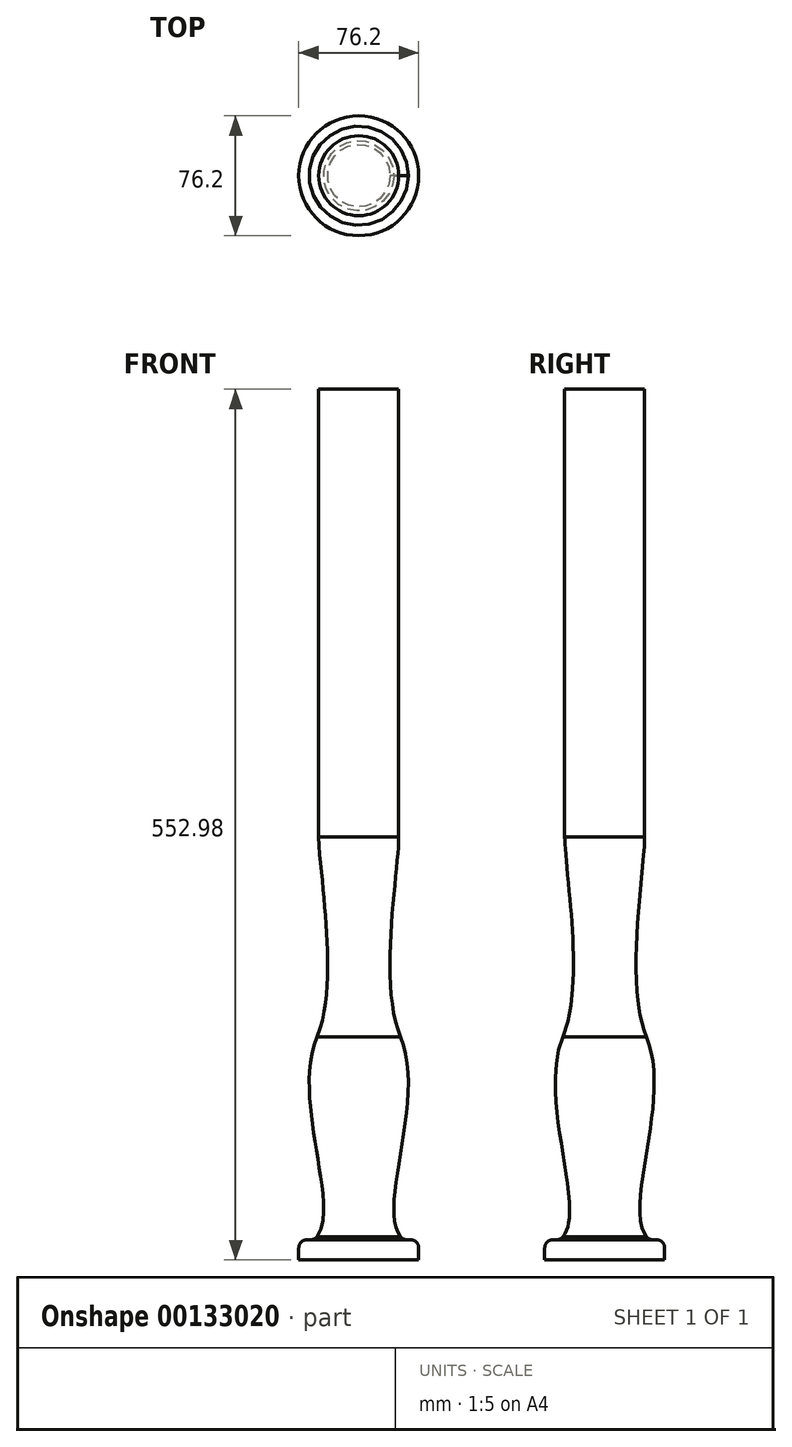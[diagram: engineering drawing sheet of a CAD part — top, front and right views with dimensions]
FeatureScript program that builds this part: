
annotation { "Feature Type Name" : "Feature", "Feature Type Description" : "" }
export const myFeature = defineFeature(function(context is Context, id is Id, definition is map)
    precondition{}
    {
        {
            var Q0;
            Q0=qCreatedBy(makeId("Front.planeOp"),FACE);
            var sketch = newSketch(context, id + "F0", { "sketchPlane" : qUnion([Q0])});
            skLineSegment(sketch, "E0.0", {"start": v(32.98, 284.37) * mm, "end": v(32.98, -255.91) * mm});
            skLineSegment(sketch, "E1", {"start": v(7.58, 284.37) * mm, "end": v(32.98, 284.37) * mm});
            skLineSegment(sketch, "E2.bottom", {"start": v(2.5, -255.91) * mm, "end": v(-0.04, -255.91) * mm});
            skLineSegment(sketch, "E2.top", {"start": v(32.98, -268.61) * mm, "end": v(-5.12, -268.61) * mm});
            skLineSegment(sketch, "E2.left", {"start": v(32.98, -255.91) * mm, "end": v(32.98, -268.61) * mm});
            skLineSegment(sketch, "E2.right", {"start": v(-5.12, -261) * mm, "end": v(-5.12, -268.61) * mm});
            skPoint(sketch, "E3.visualSharp", {"position": v(-5.12, -255.91) * mm});
            skArc(sketch, "E3.filletArc", {"start": v(-0.04, -255.91) * mm, "mid": v(-3.64, -257.4) * mm, "end": v(-5.12, -261) * mm});
            skPoint(sketch, "E4.newPointA", {"position": v(32.98, -255.91) * mm});
            skPoint(sketch, "E4.newPointB", {"position": v(-59.9, -321.48) * mm});
            skArc(sketch, "E4.filletArc", {"start": v(2.5, -255.91) * mm, "mid": v(4.7, -255.4) * mm, "end": v(6.47, -254) * mm});
            skLineSegment(sketch, "E5", {"start": v(7.58, 284.37) * mm, "end": v(7.58, 248.33) * mm});
            skFitSpline(sketch, "E6", {"points": [v(6.47, -254) * mm, v(6.47, -127) * mm], "startDerivative": vector(45.52, 57.04) * mm, "endDerivative": vector(49.7, 118.34) * mm});
            skFitSpline(sketch, "E7", {"points": [v(6.47, -127) * mm, v(7.58, 0) * mm], "startDerivative": vector(43.07, 102.58) * mm, "endDerivative": vector(0, 62.7) * mm});
            skFitSpline(sketch, "E8", {"points": [v(7.58, 0) * mm, v(7.58, 127) * mm], "startDerivative": vector(0, 131.65) * mm, "endDerivative": vector(0, 113.4) * mm});
            skFitSpline(sketch, "E9", {"points": [v(7.58, 127) * mm, v(7.58, 248.33) * mm], "startDerivative": vector(0, 127.49) * mm, "endDerivative": vector(0, 113.86) * mm});
            skSolve(sketch);
        }
        {
            var Q0;
            Q0 = qSketchRegion(id + "F0", true);
            var Q1;
            Q1=sQuery(id+"F0.wireOp",EDGE,"E0.0");
            revolve(context, id + "F1", {"entities" : qUnion([Q0]), "axis" : qUnion([Q1]), "revolveType" : RevolveType.FULL});
        }
    });
